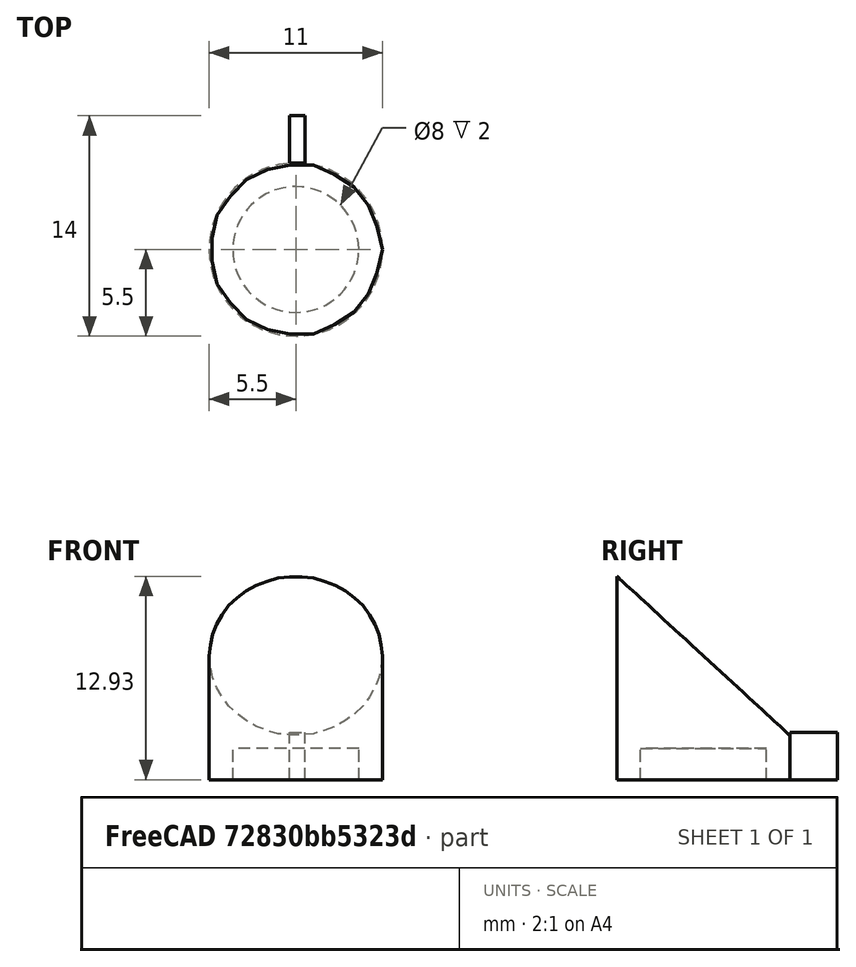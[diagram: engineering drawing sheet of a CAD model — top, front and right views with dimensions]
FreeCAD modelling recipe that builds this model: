
FCSTD DOCUMENT  (FreeCAD 0.18.4R)
Label: tappo
License: All rights reserved
LicenseURL: http://en.wikipedia.org/wiki/All_rights_reserved
objects: Part::Cylinder×3, Part::Cut×3, Part::Box×3, PartDesign::FeatureBase×1, PartDesign::Body×1, Part::Fuse×1
note: 12 computed .brp shape members not serialized (recipe doc carries the construction recipe); baked Part::Feature solids carry a one-line shape summary decoded from their .brp

FEATURE [Part::Cylinder] Cylinder
  Angle = 360
  AttacherType = Attacher::AttachEngine3D
  Height = 13
  Radius = 5.5
FEATURE [Part::Cylinder] Cylinder001
  Angle = 360
  AttacherType = Attacher::AttachEngine3D
  Height = 15
  Radius = 4
FEATURE [Part::Cut] Cut
  Base = -> Cylinder
  Tool = -> Cylinder001
FEATURE [Part::Box] Box  label="Cube"
  AttacherType = Attacher::AttachEngine3D
  Height = 13
  Length = 16
  Placement = pos=(-7.1,-7.1,14.4) rot=(-1,0,0;0.74351rad)
  Width = 22
FEATURE [PartDesign::FeatureBase] BaseFeature
  BaseFeature = -> Cut
FEATURE [PartDesign::Body] Body
  BaseFeature = -> Cut
  Group = -> [BaseFeature]
  Origin = -> Origin
  Tip = -> BaseFeature
FEATURE [Part::Box] Box001  label="Cube001"
  AttacherType = Attacher::AttachEngine3D
  Height = 3
  Length = 1
  Placement = pos=(-0.4,5.5,0) rot=(0,0,1;0rad)
  Width = 3
FEATURE [Part::Cut] Cut001
  Base = -> Body
  Tool = -> Box
FEATURE [Part::Cylinder] Cylinder002
  Angle = 360
  AttacherType = Attacher::AttachEngine3D
  Height = 15
  Placement = pos=(0,0,2) rot=(0,0,1;0rad)
  Radius = 4
FEATURE [Part::Box] Box002  label="Cube002"
  AttacherType = Attacher::AttachEngine3D
  Height = 13
  Length = 16
  Placement = pos=(-7.1,-7.1,14.4) rot=(-1,0,0;0.74351rad)
  Width = 22
FEATURE [Part::Cut] Cut002
  Base = -> Cylinder002
  Tool = -> Box002
FEATURE [Part::Fuse] Fusion
  Base = -> Cut001
  Tool = -> Cut002
